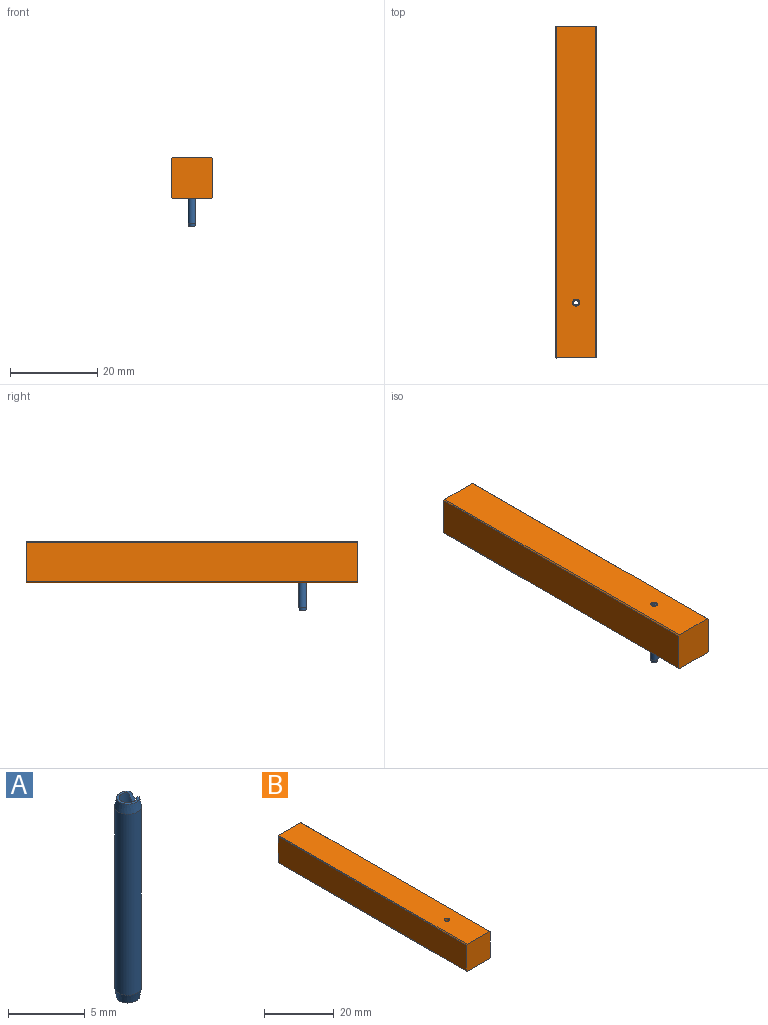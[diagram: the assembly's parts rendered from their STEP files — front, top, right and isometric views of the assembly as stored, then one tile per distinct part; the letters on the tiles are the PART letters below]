
ASSEMBLY  parts=2 mates=1
PART A: 12 faces, bbox 1.7x1.8x15.9 mm
  f0: cylinder r=0.57mm len=15.88mm, axis (0,0,-1), area 51.9mm2, adj f4,f5,f6,f7,f8,f9,f10,f11
  f1: cone r=0.81mm half-angle=10.1deg, axis (0,0,-1), area 3.3mm2, adj f2,f8,f9,f11
  f2: cylinder r=0.88mm len=14.45mm, axis (0,0,-1), area 75.3mm2, adj f1,f3,f6,f7
  f3: cone r=0.81mm half-angle=10.1deg, axis (0,0,1), area 3.3mm2, adj f2,f4,f5,f10
  f4: plane 0.71x0.46mm, normal (0,0.94,-0.34), area 0.2mm2, adj f0,f3,f7,f10
  f5: plane 0.71x0.46mm, normal (0,-0.94,-0.34), area 0.2mm2, adj f0,f3,f6,f10
  f6: plane 14.45x0.31mm, normal (0,-1,0), area 4.5mm2, adj f0,f2,f5,f9
  f7: plane 14.45x0.31mm, normal (0,1,0), area 4.5mm2, adj f0,f2,f4,f8
  f8: plane 0.71x0.46mm, normal (0,0.94,0.34), area 0.2mm2, adj f0,f1,f7,f11
  f9: plane 0.71x0.46mm, normal (0,-0.94,0.34), area 0.2mm2, adj f0,f1,f6,f11
  f10: plane 1.5x1.38mm, normal (0,0,-1), area 0.6mm2, adj f0,f3,f4,f5
  f11: plane 1.5x1.38mm, normal (0,0,1), area 0.6mm2, adj f0,f1,f8,f9
PART B: 11 faces, bbox 9.5x76.2x9.5 mm
  f0: plane 76.2x9.02mm, normal (0,0,-1), area 685.1mm2, adj f4,f5,f6,f8,f10
  f1: plane 76.2x9.02mm, normal (1,0,0), area 687.1mm2, adj f4,f5,f6,f7
  f2: plane 76.2x9.02mm, normal (0,0,1), area 685.1mm2, adj f4,f5,f7,f9,f10
  f3: plane 76.2x9.02mm, normal (-1,0,0), area 687.1mm2, adj f4,f5,f8,f9
  f4: plane 9.53x9.53mm, normal (0,-1,0), area 90.6mm2, adj f0,f1,f2,f3,f6,f7,f8,f9
  f5: plane 9.53x9.53mm, normal (0,1,0), area 90.6mm2, adj f0,f1,f2,f3,f6,f7,f8,f9
  f6: plane 76.2x0.25mm, normal (0.71,0,-0.71), area 27.4mm2, adj f0,f1,f4,f5
  f7: plane 76.2x0.25mm, normal (0.71,0,0.71), area 27.4mm2, adj f1,f2,f4,f5
  f8: plane 76.2x0.25mm, normal (-0.71,0,-0.71), area 27.4mm2, adj f0,f3,f4,f5
  f9: plane 76.2x0.25mm, normal (-0.71,0,0.71), area 27.4mm2, adj f2,f3,f4,f5
  f10: cylinder r=0.79mm len=9.53mm, axis (0,0,1), area 47.5mm2, adj f0,f2
PLACE A t=(-1.34,-3.38,4.04)mm
PLACE B t=(-1.34,60.12,-0.73)mm
MATE fastened B.f10 <-> A.f1  axis (0,0,1) through (-1.34,-3.38,4.04)mm
